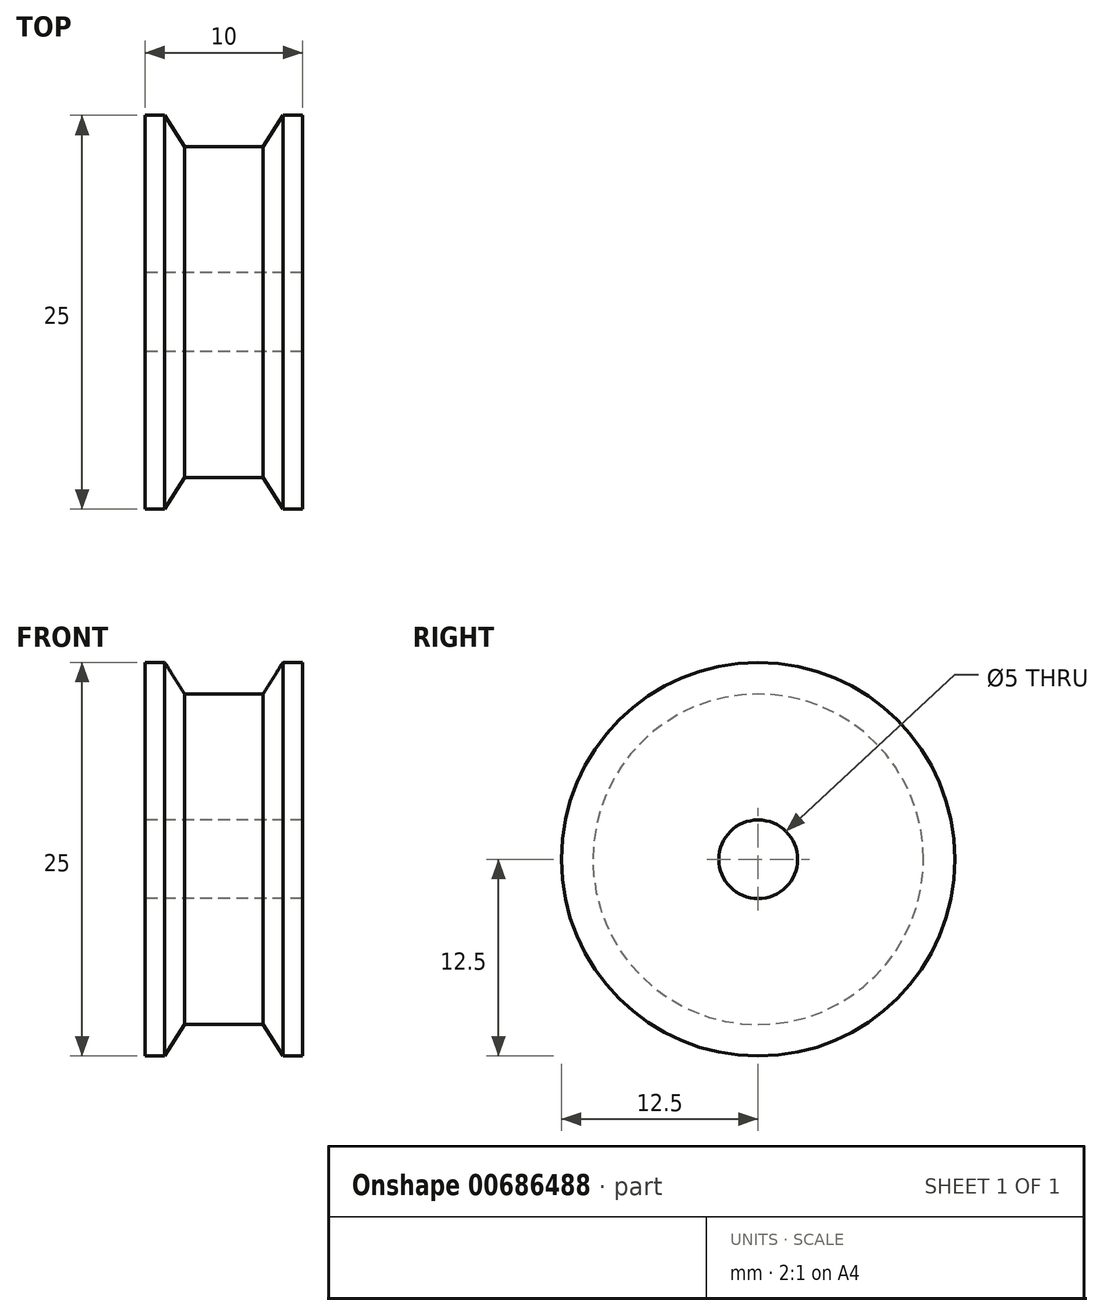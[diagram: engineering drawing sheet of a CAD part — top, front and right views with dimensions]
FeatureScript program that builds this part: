
annotation { "Feature Type Name" : "Feature", "Feature Type Description" : "" }
export const myFeature = defineFeature(function(context is Context, id is Id, definition is map)
    precondition{}
    {
        {
            var Q0;
            Q0=qCreatedBy(makeId("Front.planeOp"),FACE);
            var sketch = newSketch(context, id + "F0", { "sketchPlane" : qUnion([Q0])});
            skLineSegment(sketch, "E0.bottom", {"start": v(-5, 0) * mm, "end": v(5, 0) * mm});
            skLineSegment(sketch, "E0.left", {"start": v(-5, 0) * mm, "end": v(-5, 10) * mm});
            skLineSegment(sketch, "E0.right", {"start": v(5, 0) * mm, "end": v(5, 10) * mm});
            skLineSegment(sketch, "E1", {"start": v(-11, -2.5) * mm, "end": v(16.5, -2.5) * mm});
            skLineSegment(sketch, "E2", {"start": v(-2.5, 8) * mm, "end": v(2.5, 8) * mm});
            skLineSegment(sketch, "E3", {"start": v(-5, 10) * mm, "end": v(-3.75, 10) * mm});
            skLineSegment(sketch, "E4", {"start": v(-3.75, 10) * mm, "end": v(-2.5, 8) * mm});
            skLineSegment(sketch, "E5", {"start": v(2.5, 8) * mm, "end": v(3.75, 10) * mm});
            skLineSegment(sketch, "E6", {"start": v(3.75, 10) * mm, "end": v(5, 10) * mm});
            skSolve(sketch);
        }
        {
            var Q0;
            Q0 = qSketchRegion(id + "F0", true);
            var Q1;
            Q1=sQuery(id+"F0.wireOp",EDGE,"E1");
            revolve(context, id + "F1", {"entities" : qUnion([Q0]), "axis" : qUnion([Q1]), "revolveType" : RevolveType.FULL});
        }
    });
